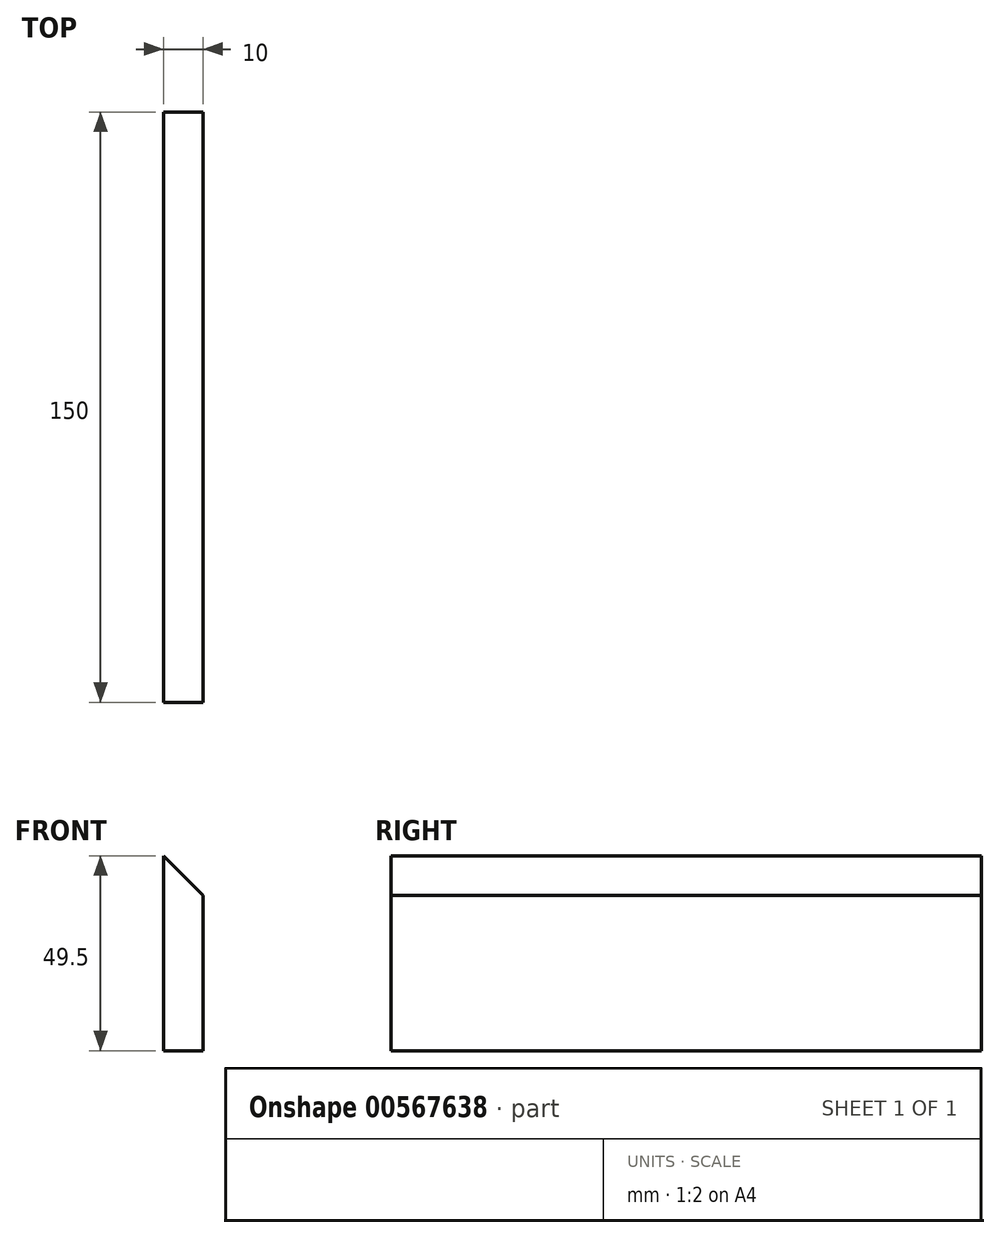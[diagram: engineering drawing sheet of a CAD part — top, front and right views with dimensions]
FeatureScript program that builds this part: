
annotation { "Feature Type Name" : "Feature", "Feature Type Description" : "" }
export const myFeature = defineFeature(function(context is Context, id is Id, definition is map)
    precondition{}
    {
        {
            var Q0;
            Q0=qCreatedBy(makeId("Front.planeOp"),FACE);
            var sketch = newSketch(context, id + "F0", { "sketchPlane" : qUnion([Q0])});
            skLineSegment(sketch, "E0", {"start": v(0, 49.5) * mm, "end": v(0, 0) * mm});
            skLineSegment(sketch, "E1", {"start": v(0, 0) * mm, "end": v(10, 0) * mm});
            skLineSegment(sketch, "E2", {"start": v(10, 0) * mm, "end": v(10, 39.5) * mm});
            skLineSegment(sketch, "E3", {"start": v(10, 39.5) * mm, "end": v(0, 49.5) * mm});
            skSolve(sketch);
        }
        {
            var Q0;
            Q0=makeQuery(id+"F0.imprint","IMPRINT",FACE,{"disambiguationData":[TD([[makeQuery(id+"F0.imprint","IMPRINT",EDGE,{"derivedFrom":sQuery(id+"F0.wireOp",EDGE,"E0")}),1.0]])]});
            extrude(context, id + "F1", {"entities" : qUnion([Q0]), "depth" : 150 * mm, "offsetDistance" : 25 * mm});
        }
        {
            var Q0;
            Q0=makeQuery(id+"F1.opExtrude","SWEPT_FACE",FACE,{"disambiguationData":[OSD([sQuery(id+"F0.wireOp",EDGE,"E3")])]});
            var sketch = newSketch(context, id + "F2", { "sketchPlane" : qUnion([Q0])});
            skPoint(sketch, "E4.endSnap0", {"position": v(-27.93, 0) * mm});
            skLineSegment(sketch, "E5", {"start": v(-30, -150) * mm, "end": v(-30, -130) * mm});
            skLineSegment(sketch, "E6", {"start": v(-30, 0) * mm, "end": v(-30, -20) * mm});
            skSolve(sketch);
        }
        {
            var Q0;
            Q0=sQuery(id+"F2.wireOp",VERTEX,"E5.end");
            var Q1;
            Q1=sQuery(id+"F2.wireOp",VERTEX,"E6.end");
            var Q2;
            Q2=makeQuery(id+"F1.opExtrude","SWEPT_BODY",BODY,{"disambiguationData":[OSD([sQuery(id+"F0.wireOp",EDGE,"E0"),sQuery(id+"F0.wireOp",EDGE,"E1"),sQuery(id+"F0.wireOp",EDGE,"E2"),sQuery(id+"F0.wireOp",EDGE,"E3")])]});
            hole(context, id + "F3", {"style" : HoleStyle.SIMPLE, "endStyle" : HoleEndStyle.BLIND, "standardTappedOrClearance" : lookupTablePath({ "standard" : "ISO", "fit" : "Normal", "size" : "M4", "type" : "Clearance" }), "standardBlindInLast" : lookupTablePath({ "fit" : "Standard", "standard" : "ISO", "size" : "M4", "type" : "Clearance" }), "holeDiameter" : 4.4 * mm, "holeDepth" : 14.1 * mm, "isTappedThrough" : true, "tappedDepth" : 12 * mm, "tapClearance" : 3, "locations" : qUnion([Q0, Q1]), "scope" : qUnion([Q2])});
        }
    });
